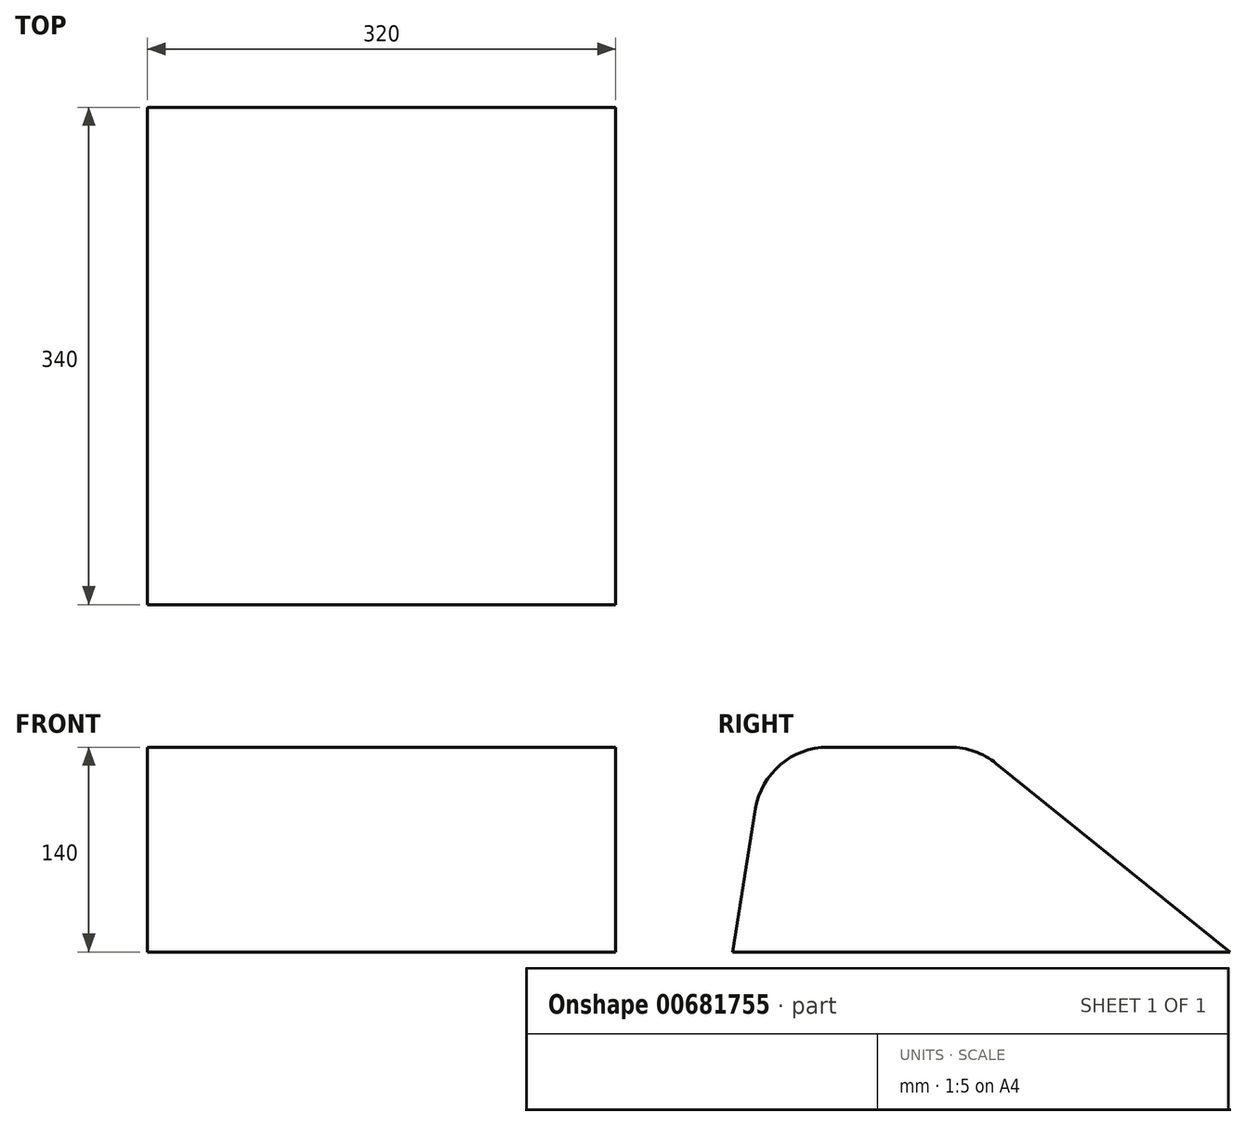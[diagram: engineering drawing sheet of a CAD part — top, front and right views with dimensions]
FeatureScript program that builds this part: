
annotation { "Feature Type Name" : "Feature", "Feature Type Description" : "" }
export const myFeature = defineFeature(function(context is Context, id is Id, definition is map)
    precondition{}
    {
        {
            var Q0;
            Q0=qCreatedBy(makeId("Right.planeOp"),FACE);
            var sketch = newSketch(context, id + "F0", { "sketchPlane" : qUnion([Q0])});
            skLineSegment(sketch, "E0", {"start": v(0, 0) * mm, "end": v(340, 0) * mm});
            skLineSegment(sketch, "E1", {"start": v(340, 0) * mm, "end": v(180.18, 128.92) * mm});
            skLineSegment(sketch, "E2", {"start": v(0, 0) * mm, "end": v(15.74, 97.93) * mm});
            skLineSegment(sketch, "E3", {"start": v(65.1, 140) * mm, "end": v(148.79, 140) * mm});
            skPoint(sketch, "E4.visualSharp", {"position": v(166.44, 140) * mm});
            skArc(sketch, "E4.filletArc", {"start": v(167.81, 138.9) * mm, "mid": v(166.34, 139.71) * mm, "end": v(164.67, 140) * mm});
            skArc(sketch, "E5.filletArc", {"start": v(180.18, 128.92) * mm, "mid": v(165.43, 137.15) * mm, "end": v(148.79, 140) * mm});
            skPoint(sketch, "E6.visualSharp", {"position": v(22.5, 140) * mm});
            skArc(sketch, "E6.filletArc", {"start": v(65.1, 140) * mm, "mid": v(32.68, 128.06) * mm, "end": v(15.74, 97.93) * mm});
            skSolve(sketch);
        }
        {
            var Q0;
            Q0 = qSketchRegion(id + "F0", true);
            extrude(context, id + "F1", {"entities" : qUnion([Q0]), "depth" : 320 * mm, "offsetDistance" : 25 * mm});
        }
    });
